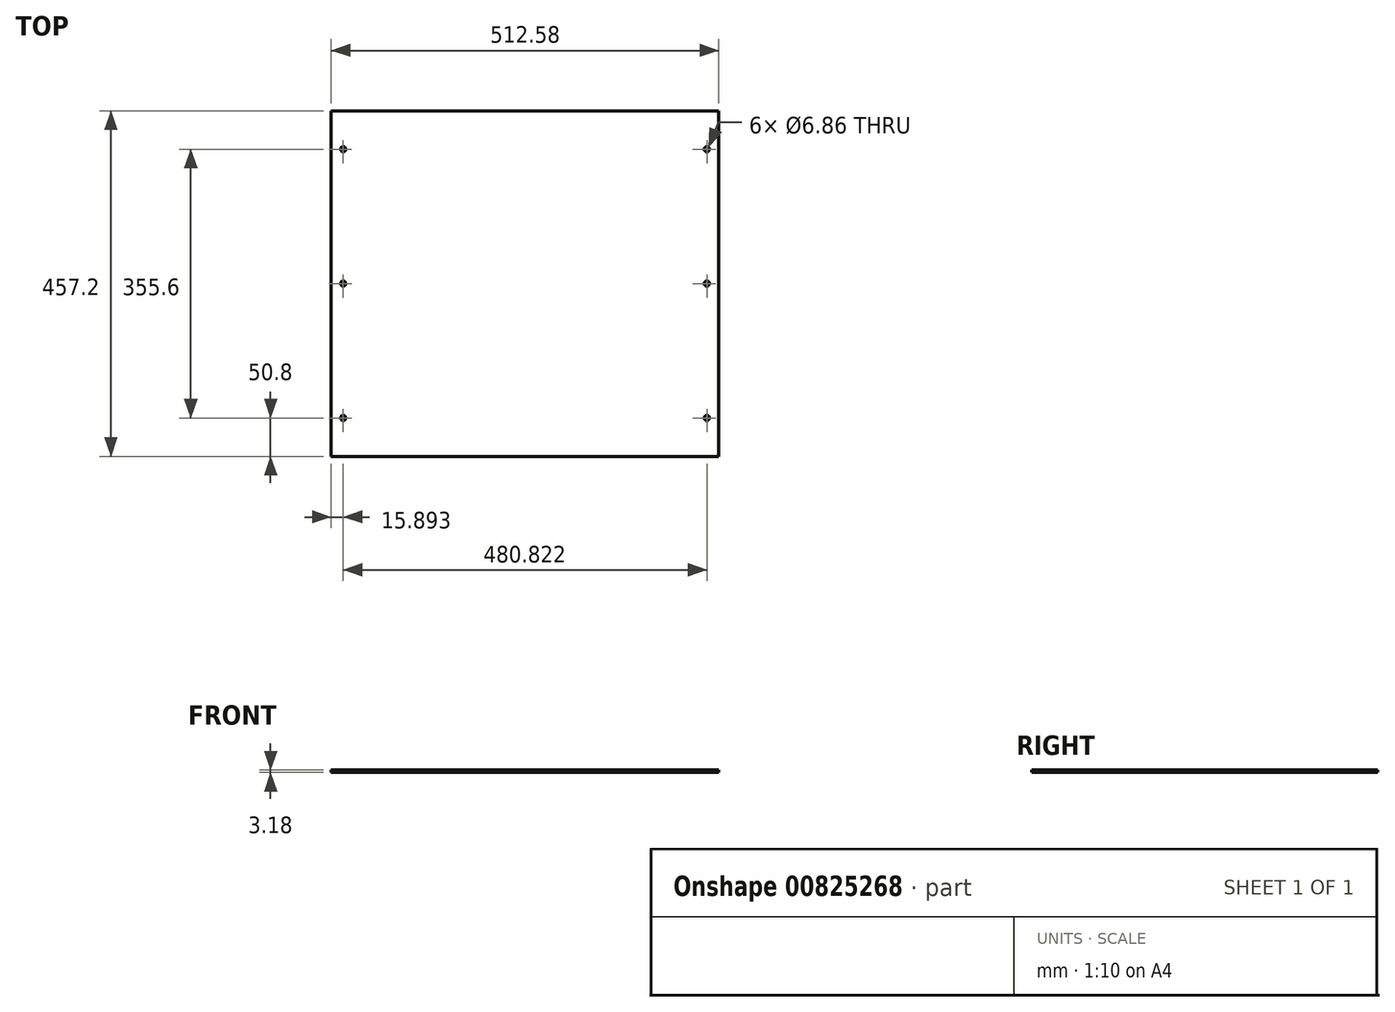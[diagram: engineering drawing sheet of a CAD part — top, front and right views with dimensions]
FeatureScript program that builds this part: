
annotation { "Feature Type Name" : "Feature", "Feature Type Description" : "" }
export const myFeature = defineFeature(function(context is Context, id is Id, definition is map)
    precondition{}
    {
        {
            var Q0;
            Q0=qCreatedBy(makeId("Top.planeOp"),FACE);
            var sketch = newSketch(context, id + "F0", { "sketchPlane" : qUnion([Q0])});
            skLineSegment(sketch, "E0.bottom", {"start": v(0, 0) * mm, "end": v(531.62, 0) * mm});
            skLineSegment(sketch, "E0.top", {"start": v(0, 457.2) * mm, "end": v(531.62, 457.2) * mm});
            skLineSegment(sketch, "E0.left", {"start": v(0, 0) * mm, "end": v(0, 457.2) * mm});
            skLineSegment(sketch, "E0.right", {"start": v(531.62, 0) * mm, "end": v(531.62, 457.2) * mm});
            skCircle(sketch, "E1", {"center": v(25.41, 406.4) * mm, "radius": 3.43 * mm});
            skCircle(sketch, "E2", {"center": v(25.41, 228.6) * mm, "radius": 3.43 * mm});
            skCircle(sketch, "E3", {"center": v(25.41, 50.8) * mm, "radius": 3.43 * mm});
            skCircle(sketch, "E4", {"center": v(506.23, 50.8) * mm, "radius": 3.43 * mm});
            skCircle(sketch, "E5", {"center": v(506.23, 228.6) * mm, "radius": 3.43 * mm});
            skCircle(sketch, "E6", {"center": v(506.23, 406.4) * mm, "radius": 3.43 * mm});
            skLineSegment(sketch, "E7", {"start": v(9.53, 0) * mm, "end": v(9.52, 457.2) * mm});
            skLineSegment(sketch, "E8", {"start": v(522.1, 457.2) * mm, "end": v(522.1, 0) * mm});
            skSolve(sketch);
        }
        {
            var Q0;
            Q0=makeQuery(id+"F0.imprint","IMPRINT",FACE,{"disambiguationData":[TD([[makeQuery(id+"F0.imprint","IMPRINT",EDGE,{"derivedFrom":sQuery(id+"F0.wireOp",EDGE,"E1")}),-1.0]])]});
            extrude(context, id + "F1", {"entities" : qUnion([Q0]), "depth" : 3.17 * mm, "offsetDistance" : 25.4 * mm});
        }
    });
